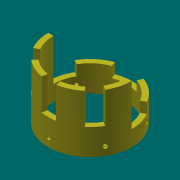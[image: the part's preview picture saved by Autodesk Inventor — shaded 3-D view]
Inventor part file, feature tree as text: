
AUTODESK INVENTOR PART (.ipt)
format: ipt  version: 2013 (Build 170138000, 138)  size: 285,696 bytes
history: native  units: mm
features: sketch x16, extrude x14, other x2, hole x2, pattern_circular x1
ambient origin geometry x8: Origin, YZ Plane, XZ Plane, XY Plane, X Axis, Y Axis, Z Axis, Center Point
feature tree (35):
  other  "ソリッド1"
  extrude  "押し出し1"  Depth=90.0mm
  extrude  "押し出し2"  Depth=80.0mm
  extrude  "押し出し3"  Depth=5.0mm TaperAngle=0.0deg
  extrude  "押し出し4"  Depth=80.0mm
  extrude  "押し出し5"  Depth=100.0mm TaperAngle=0.0deg
  extrude  "押し出し6"  Depth=70.0mm
  extrude  "押し出し7"  Depth=100.0mm TaperAngle=0.0deg
  extrude  "押し出し8"  Depth=55.0mm
  extrude  "押し出し9"  Depth=5.0mm TaperAngle=0.0deg
  hole  "穴1"  [1 undecoded]
  extrude  "押し出し10"  Depth=40.0mm TaperAngle=0.0deg
  extrude  "押し出し11"  Depth=13.962634mm
  other  "作業平面1"
  hole  "穴2"  [1 undecoded]
  pattern_circular  "円形状パターン1"  Angle=150.0deg  [1 undecoded]
  extrude  "押し出し12"  Depth=11.34464mm
  extrude  "押し出し13"  TaperAngle=30.0deg  [1 undecoded]
  extrude  "押し出し14"  Depth=40.0mm TaperAngle=0.0deg
  sketch  "スケッチ1"
  sketch  "スケッチ2"
  sketch  "スケッチ3"
  sketch  "スケッチ4"
  sketch  "スケッチ5"
  sketch  "スケッチ6"
  sketch  "スケッチ7"
  sketch  "スケッチ8"
  sketch  "スケッチ9"
  sketch  "スケッチ10"
  sketch  "スケッチ11"
  sketch  "スケッチ12"
  sketch  "スケッチ13"
  sketch  "スケッチ14"
  sketch  "スケッチ15"
  sketch  "スケッチ16"
note: 4 required parameter values undecoded (feature->parameter linkage not recoverable at this tier; creation-order binding heuristic only, values carry confidence <= 0.55)
